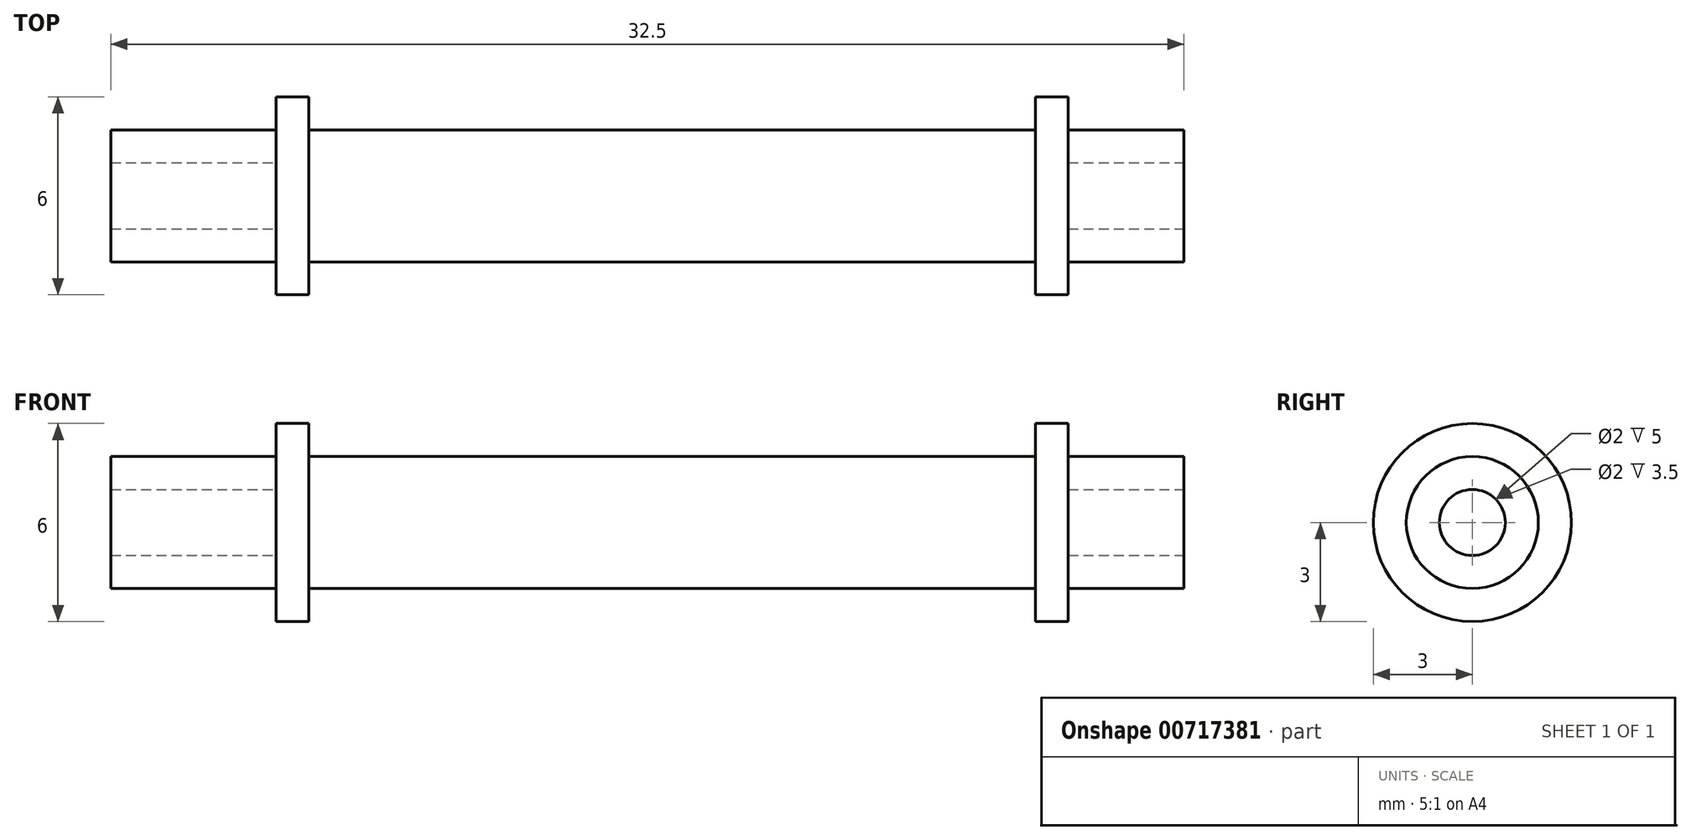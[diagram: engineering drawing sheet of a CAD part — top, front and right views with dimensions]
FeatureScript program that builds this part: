
annotation { "Feature Type Name" : "Feature", "Feature Type Description" : "" }
export const myFeature = defineFeature(function(context is Context, id is Id, definition is map)
    precondition{}
    {
        {
            var Q0;
            Q0=qCreatedBy(makeId("Front.planeOp"),FACE);
            var sketch = newSketch(context, id + "F0", { "sketchPlane" : qUnion([Q0])});
            skLineSegment(sketch, "E0", {"start": v(-15, 1) * mm, "end": v(-15, 2) * mm});
            skLineSegment(sketch, "E1", {"start": v(-15, 2) * mm, "end": v(-10, 2) * mm});
            skLineSegment(sketch, "E2", {"start": v(-10, 2) * mm, "end": v(-10, 3) * mm});
            skLineSegment(sketch, "E3", {"start": v(-10, 3) * mm, "end": v(-9, 3) * mm});
            skLineSegment(sketch, "E4", {"start": v(-9, 3) * mm, "end": v(-9, 2) * mm});
            skLineSegment(sketch, "E5", {"start": v(-9, 2) * mm, "end": v(0, 2) * mm});
            skLineSegment(sketch, "E6", {"start": v(-15, 1) * mm, "end": v(-10, 1) * mm});
            skLineSegment(sketch, "E7", {"start": v(-10, 1) * mm, "end": v(-10, 0) * mm});
            skLineSegment(sketch, "E8", {"start": v(0, 2) * mm, "end": v(13, 2) * mm});
            skLineSegment(sketch, "E9", {"start": v(13, 2) * mm, "end": v(13, 3) * mm});
            skLineSegment(sketch, "E10", {"start": v(13, 3) * mm, "end": v(14, 3) * mm});
            skLineSegment(sketch, "E11", {"start": v(14, 3) * mm, "end": v(14, 2) * mm});
            skLineSegment(sketch, "E12", {"start": v(14, 2) * mm, "end": v(17.5, 2) * mm});
            skLineSegment(sketch, "E13", {"start": v(17.5, 2) * mm, "end": v(17.5, 1) * mm});
            skLineSegment(sketch, "E14", {"start": v(17.5, 1) * mm, "end": v(14, 1) * mm});
            skLineSegment(sketch, "E15", {"start": v(14, 1) * mm, "end": v(14, 0) * mm});
            skLineSegment(sketch, "E16", {"start": v(14, 0) * mm, "end": v(-10, 0) * mm});
            skSolve(sketch);
        }
        {
            var Q0;
            Q0=makeQuery(id+"F0.imprint","IMPRINT",FACE,{"disambiguationData":[TD([[makeQuery(id+"F0.imprint","IMPRINT",EDGE,{"derivedFrom":sQuery(id+"F0.wireOp",EDGE,"E0")}),-1.0]])]});
            var Q1;
            Q1=sQuery(id+"F0.wireOp",EDGE,"E16");
            revolve(context, id + "F1", {"surfaceOperationType" : NewSurfaceOperationType.NEW, "entities" : qUnion([Q0]), "axis" : qUnion([Q1]), "revolveType" : RevolveType.FULL});
        }
    });
